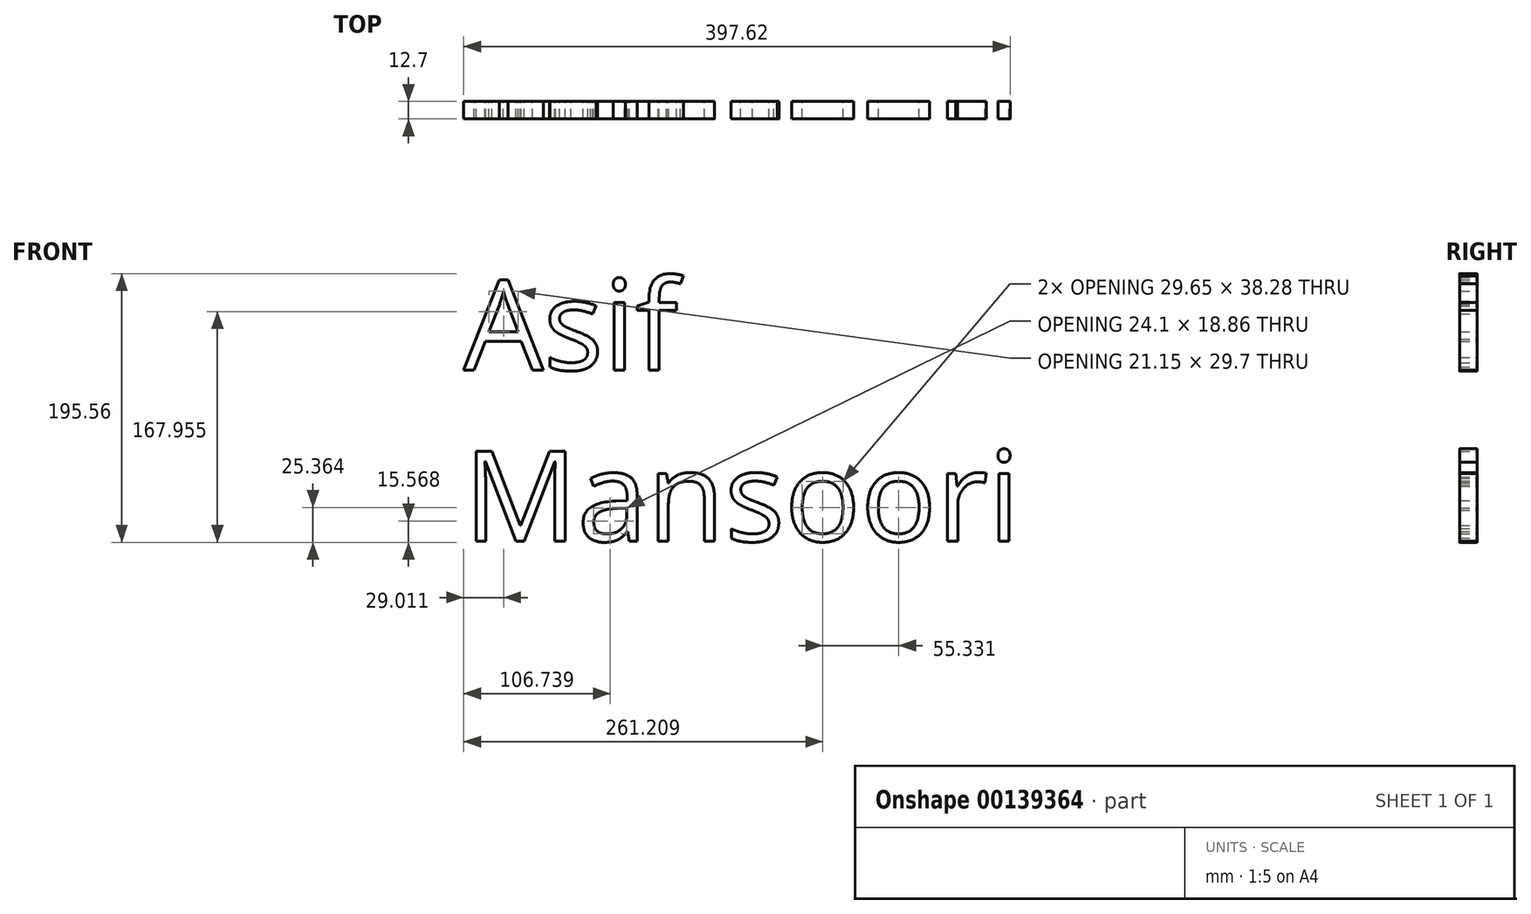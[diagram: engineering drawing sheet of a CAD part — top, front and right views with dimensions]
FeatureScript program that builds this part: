
annotation { "Feature Type Name" : "Feature", "Feature Type Description" : "" }
export const myFeature = defineFeature(function(context is Context, id is Id, definition is map)
    precondition{}
    {
        {
            var Q0;
            Q0=qCreatedBy(makeId("Front.planeOp"),FACE);
            var sketch = newSketch(context, id + "F0", { "sketchPlane" : qUnion([Q0])});
            skText(sketch, "E0", { "text": "Asif \nMansoori", "fontName": "OpenSans-Regular.ttf"});
            const initialGuessF0  = {"E0": [-0.06883, 0, 1, 0, 0.06595]};
            skSetInitialGuess(sketch, initialGuessF0);
            skSolve(sketch);
        }
        {
            var Q0;
            Q0=makeQuery(id+"F0.imprint","IMPRINT",FACE,{"disambiguationData":[TD([[makeQuery(id+"F0.imprint","IMPRINT",EDGE,{"derivedFrom":sQuery(id+"F0.wireOp",EDGE,"E0.sketch_text.stroke-0")}),-1.0]])]});
            var Q1;
            Q1=makeQuery(id+"F0.imprint","IMPRINT",FACE,{"disambiguationData":[TD([[makeQuery(id+"F0.imprint","IMPRINT",EDGE,{"derivedFrom":sQuery(id+"F0.wireOp",EDGE,"E0.sketch_text.stroke-13")}),-1.0]])]});
            var Q2;
            Q2=makeQuery(id+"F0.imprint","IMPRINT",FACE,{"disambiguationData":[TD([[makeQuery(id+"F0.imprint","IMPRINT",EDGE,{"derivedFrom":sQuery(id+"F0.wireOp",EDGE,"E0.sketch_text.stroke-38")}),-1.0]])]});
            var Q3;
            Q3=makeQuery(id+"F0.imprint","IMPRINT",FACE,{"disambiguationData":[TD([[makeQuery(id+"F0.imprint","IMPRINT",EDGE,{"derivedFrom":sQuery(id+"F0.wireOp",EDGE,"E0.sketch_text.stroke-42")}),-1.0]])]});
            var Q4;
            Q4=makeQuery(id+"F0.imprint","IMPRINT",FACE,{"disambiguationData":[TD([[makeQuery(id+"F0.imprint","IMPRINT",EDGE,{"derivedFrom":sQuery(id+"F0.wireOp",EDGE,"E0.sketch_text.stroke-50")}),-1.0]])]});
            var Q5;
            Q5=makeQuery(id+"F0.imprint","IMPRINT",FACE,{"disambiguationData":[TD([[makeQuery(id+"F0.imprint","IMPRINT",EDGE,{"derivedFrom":sQuery(id+"F0.wireOp",EDGE,"E0.sketch_text.stroke-67")}),-1.0]])]});
            var Q6;
            Q6=makeQuery(id+"F0.imprint","IMPRINT",FACE,{"disambiguationData":[TD([[makeQuery(id+"F0.imprint","IMPRINT",EDGE,{"derivedFrom":sQuery(id+"F0.wireOp",EDGE,"E0.sketch_text.stroke-85")}),-1.0]])]});
            var Q7;
            Q7=makeQuery(id+"F0.imprint","IMPRINT",FACE,{"disambiguationData":[TD([[makeQuery(id+"F0.imprint","IMPRINT",EDGE,{"derivedFrom":sQuery(id+"F0.wireOp",EDGE,"E0.sketch_text.stroke-112")}),-1.0]])]});
            var Q8;
            Q8=makeQuery(id+"F0.imprint","IMPRINT",FACE,{"disambiguationData":[TD([[makeQuery(id+"F0.imprint","IMPRINT",EDGE,{"derivedFrom":sQuery(id+"F0.wireOp",EDGE,"E0.sketch_text.stroke-129")}),-1.0]])]});
            var Q9;
            Q9=makeQuery(id+"F0.imprint","IMPRINT",FACE,{"disambiguationData":[TD([[makeQuery(id+"F0.imprint","IMPRINT",EDGE,{"derivedFrom":sQuery(id+"F0.wireOp",EDGE,"E0.sketch_text.stroke-154")}),-1.0]])]});
            var Q10;
            Q10=makeQuery(id+"F0.imprint","IMPRINT",FACE,{"disambiguationData":[TD([[makeQuery(id+"F0.imprint","IMPRINT",EDGE,{"derivedFrom":sQuery(id+"F0.wireOp",EDGE,"E0.sketch_text.stroke-171")}),-1.0]])]});
            var Q11;
            Q11=makeQuery(id+"F0.imprint","IMPRINT",FACE,{"disambiguationData":[TD([[makeQuery(id+"F0.imprint","IMPRINT",EDGE,{"derivedFrom":sQuery(id+"F0.wireOp",EDGE,"E0.sketch_text.stroke-188")}),-1.0]])]});
            var Q12;
            Q12=makeQuery(id+"F0.imprint","IMPRINT",FACE,{"disambiguationData":[TD([[makeQuery(id+"F0.imprint","IMPRINT",EDGE,{"derivedFrom":sQuery(id+"F0.wireOp",EDGE,"E0.sketch_text.stroke-201")}),-1.0]])]});
            var Q13;
            Q13=makeQuery(id+"F0.imprint","IMPRINT",FACE,{"disambiguationData":[TD([[makeQuery(id+"F0.imprint","IMPRINT",EDGE,{"derivedFrom":sQuery(id+"F0.wireOp",EDGE,"E0.sketch_text.stroke-205")}),-1.0]])]});
            extrude(context, id + "F1", {"entities" : qUnion([Q0, Q1, Q2, Q3, Q4, Q5, Q6, Q7, Q8, Q9, Q10, Q11, Q12, Q13]), "depth" : 12.7 * mm});
        }
    });
